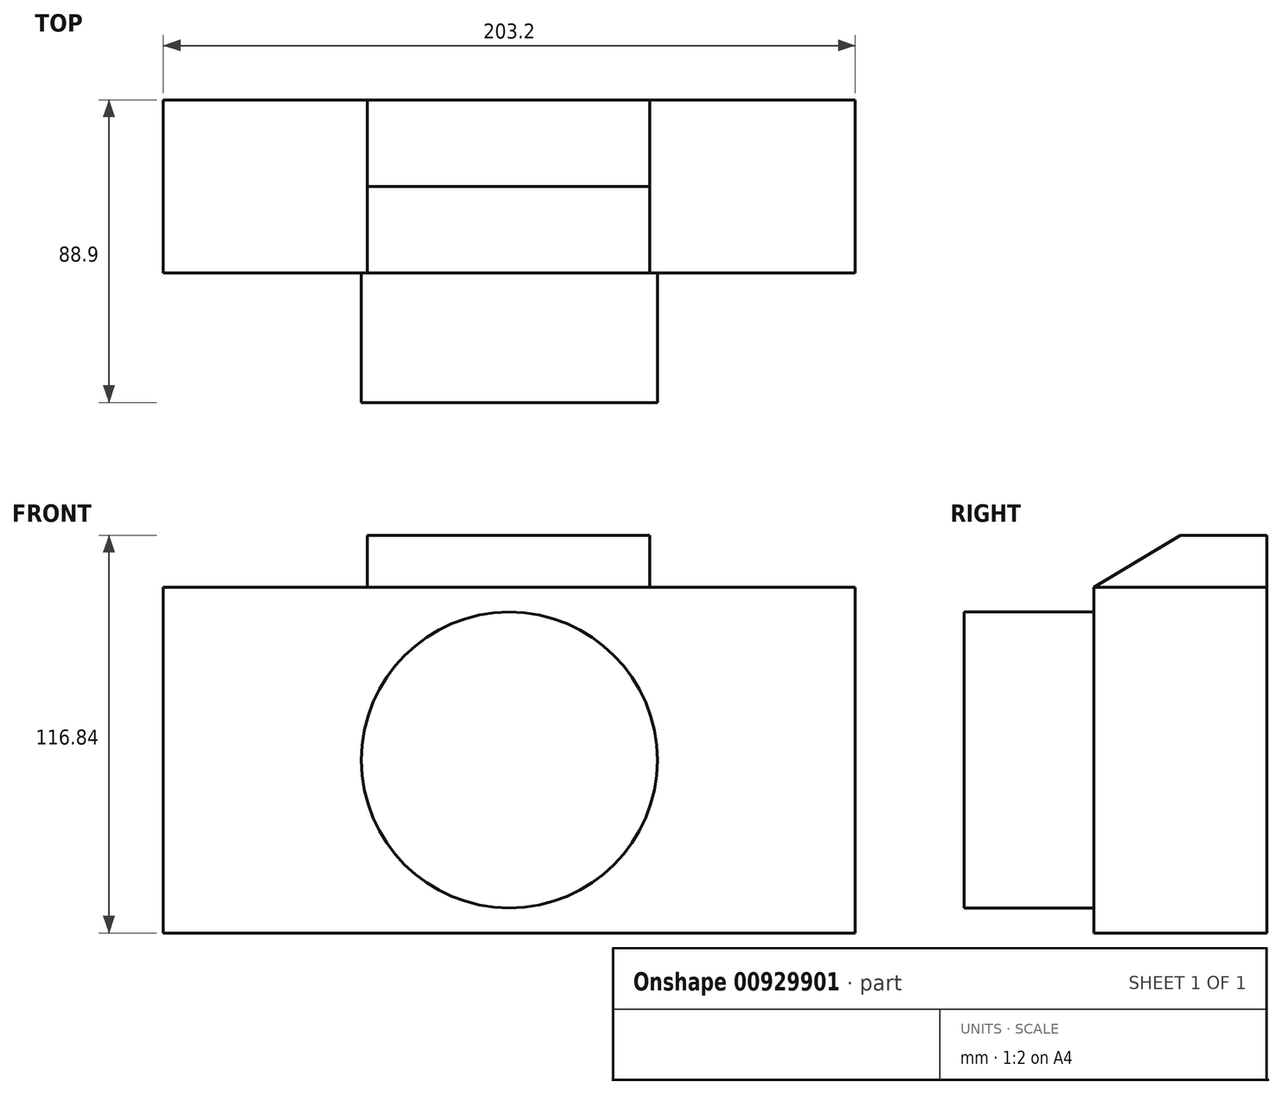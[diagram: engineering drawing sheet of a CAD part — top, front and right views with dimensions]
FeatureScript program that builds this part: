
annotation { "Feature Type Name" : "Feature", "Feature Type Description" : "" }
export const myFeature = defineFeature(function(context is Context, id is Id, definition is map)
    precondition{}
    {
        {
            var Q0;
            Q0=qCreatedBy(makeId("Top.planeOp"),FACE);
            var sketch = newSketch(context, id + "F0", { "sketchPlane" : qUnion([Q0])});
            skLineSegment(sketch, "E0.bottom", {"start": v(-114.65, -38.84) * mm, "end": v(88.55, -38.84) * mm});
            skLineSegment(sketch, "E0.top", {"start": v(-114.65, -89.64) * mm, "end": v(88.55, -89.64) * mm});
            skLineSegment(sketch, "E0.left", {"start": v(-114.65, -38.84) * mm, "end": v(-114.65, -89.64) * mm});
            skLineSegment(sketch, "E0.right", {"start": v(88.55, -38.84) * mm, "end": v(88.55, -89.64) * mm});
            skSolve(sketch);
        }
        {
            var Q0;
            Q0 = qSketchRegion(id + "F0", true);
            var Q1;
            Q1=makeQuery(id+"F0.imprint","IMPRINT",FACE,{"disambiguationData":[TD([[makeQuery(id+"F0.imprint","IMPRINT",EDGE,{"derivedFrom":sQuery(id+"F0.wireOp",EDGE,"E0.bottom")}),-1.0]])]});
            extrude(context, id + "F1", {"entities" : qUnion([Q0, Q1]), "depth" : 101.6 * mm, "offsetDistance" : 25.4 * mm});
        }
        {
            var Q0;
            Q0=makeQuery(id+"F1.opExtrude","SWEPT_FACE",FACE,{"disambiguationData":[OSD([sQuery(id+"F0.wireOp",EDGE,"E0.top")])]});
            var sketch = newSketch(context, id + "F2", { "sketchPlane" : qUnion([Q0])});
            skCircle(sketch, "E1", {"center": v(-13.05, 50.8) * mm, "radius": 43.46 * mm});
            skPoint(sketch, "E1.centerSnap0", {"position": v(88.55, 50.8) * mm});
            skPoint(sketch, "E1.centerSnap1", {"position": v(-13.05, 0) * mm});
            skSolve(sketch);
        }
        {
            var Q0;
            Q0 = qSketchRegion(id + "F2", true);
            var Q1;
            Q1=makeQuery(id+"F2.imprint","IMPRINT",FACE,{"disambiguationData":[TD([[makeQuery(id+"F2.imprint","IMPRINT",EDGE,{"derivedFrom":sQuery(id+"F2.wireOp",EDGE,"E1")}),1.0]])]});
            extrude(context, id + "F3", {"entities" : qUnion([Q0, Q1]), "operationType" : NewBodyOperationType.ADD, "depth" : 38.1 * mm, "offsetDistance" : 25.4 * mm});
        }
        {
            var Q0;
            Q0=makeQuery(id+"F1.opExtrude","CAP_FACE",FACE,{"disambiguationData":[OSD([sQuery(id+"F0.wireOp",EDGE,"E0.bottom"),sQuery(id+"F0.wireOp",EDGE,"E0.top"),sQuery(id+"F0.wireOp",EDGE,"E0.left"),sQuery(id+"F0.wireOp",EDGE,"E0.right")])],"isStart":false});
            var sketch = newSketch(context, id + "F4", { "sketchPlane" : qUnion([Q0])});
            skLineSegment(sketch, "E2.bottom", {"start": v(-54.75, -89.64) * mm, "end": v(28.12, -89.64) * mm});
            skLineSegment(sketch, "E2.top", {"start": v(-54.75, -38.84) * mm, "end": v(28.12, -38.84) * mm});
            skLineSegment(sketch, "E2.left", {"start": v(-54.75, -89.64) * mm, "end": v(-54.75, -38.84) * mm});
            skLineSegment(sketch, "E2.right", {"start": v(28.12, -89.64) * mm, "end": v(28.12, -38.84) * mm});
            skSolve(sketch);
        }
        {
            var Q0;
            Q0=makeQuery(id+"F4.imprint","IMPRINT",FACE,{"disambiguationData":[TD([[makeQuery(id+"F4.imprint","IMPRINT",EDGE,{"derivedFrom":sQuery(id+"F4.wireOp",EDGE,"E2.bottom")}),1.0]])]});
            extrude(context, id + "F5", {"entities" : qUnion([Q0]), "operationType" : NewBodyOperationType.ADD, "depth" : 15.24 * mm, "offsetDistance" : 25.4 * mm});
        }
        {
            var Q0;
            Q0=makeQuery(id+"F5.opExtrude","SWEPT_FACE",FACE,{"disambiguationData":[OSD([sQuery(id+"F4.wireOp",EDGE,"E2.right")])]});
            var sketch = newSketch(context, id + "F6", { "sketchPlane" : qUnion([Q0])});
            skLineSegment(sketch, "E3", {"start": v(-89.64, 101.6) * mm, "end": v(-64.24, 116.84) * mm});
            skLineSegment(sketch, "E4", {"start": v(-64.24, 116.84) * mm, "end": v(-89.64, 116.84) * mm});
            skLineSegment(sketch, "E5", {"start": v(-89.64, 116.84) * mm, "end": v(-89.64, 101.6) * mm});
            skSolve(sketch);
        }
        {
            var Q0;
            Q0=makeQuery(id+"F6.imprint","IMPRINT",FACE,{"disambiguationData":[TD([[makeQuery(id+"F6.imprint","IMPRINT",EDGE,{"derivedFrom":sQuery(id+"F6.wireOp",EDGE,"E3")}),1.0]])]});
            extrude(context, id + "F7", {"entities" : qUnion([Q0]), "operationType" : NewBodyOperationType.REMOVE, "oppositeDirection" : true, "depth" : 101.6 * mm, "offsetDistance" : 25.4 * mm});
        }
    });
